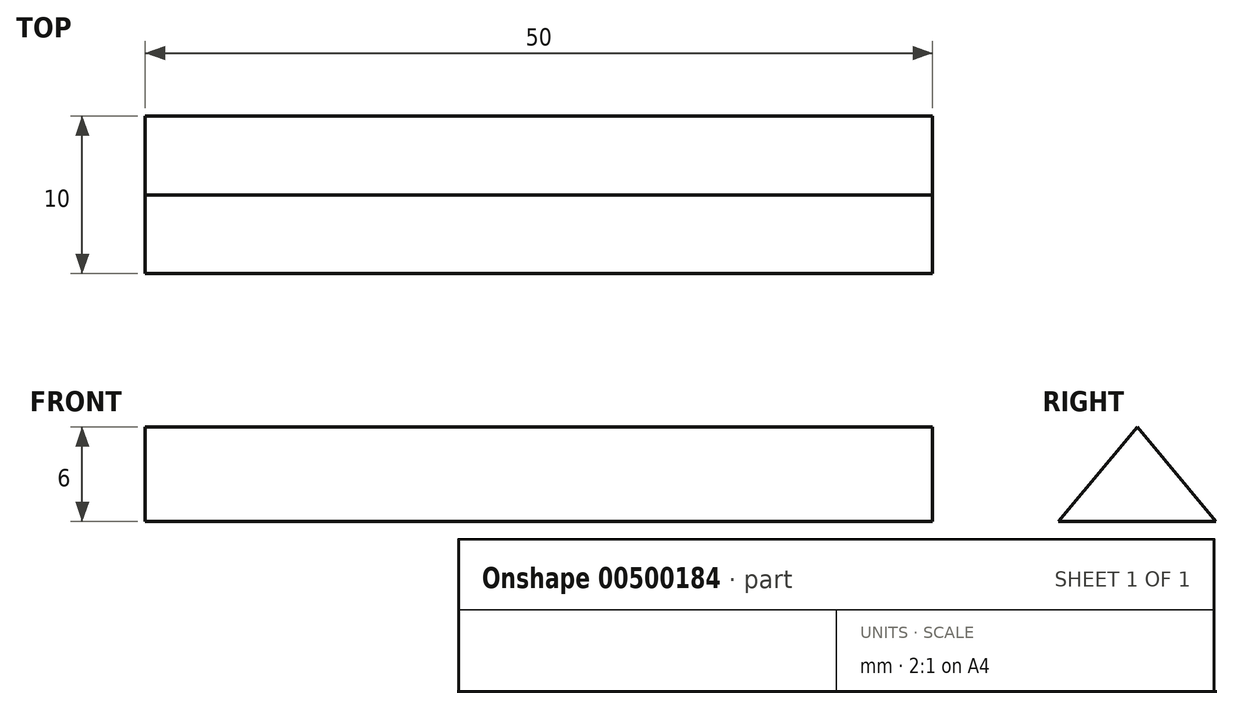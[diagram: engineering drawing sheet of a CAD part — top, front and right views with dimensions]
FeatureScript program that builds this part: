
annotation { "Feature Type Name" : "Feature", "Feature Type Description" : "" }
export const myFeature = defineFeature(function(context is Context, id is Id, definition is map)
    precondition{}
    {
        {
            var Q0;
            Q0=qCreatedBy(makeId("Right.planeOp"),FACE);
            var sketch = newSketch(context, id + "F0", { "sketchPlane" : qUnion([Q0])});
            skLineSegment(sketch, "E0", {"start": v(-5, 0) * mm, "end": v(0, 6) * mm});
            skLineSegment(sketch, "E1", {"start": v(0, 6) * mm, "end": v(5, 0) * mm});
            skLineSegment(sketch, "E2", {"start": v(5, 0) * mm, "end": v(-5, 0) * mm});
            skSolve(sketch);
        }
        {
            var Q0;
            Q0=makeQuery(id+"F0.imprint","IMPRINT",FACE,{"disambiguationData":[TD([[makeQuery(id+"F0.imprint","IMPRINT",EDGE,{"derivedFrom":sQuery(id+"F0.wireOp",EDGE,"E0")}),-1.0]])]});
            extrude(context, id + "F1", {"entities" : qUnion([Q0]), "depth" : 50 * mm});
        }
    });
